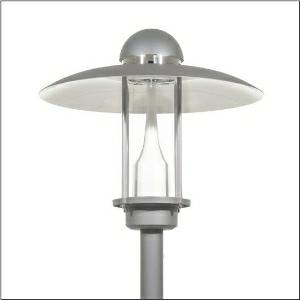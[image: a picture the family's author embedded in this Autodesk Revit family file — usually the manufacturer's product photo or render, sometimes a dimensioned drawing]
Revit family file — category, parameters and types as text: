
# Revit family: city-light_elegance_iq___p1_0a_5xa5265nf14hp_aba6
name_source: partatom
category: Lighting Fixtures
units: mm (PartAtom-declared; Revit-internal decimal feet)

## family parameters
Cut with Voids When Loaded = No
Host = Face
Light Source = No
Part Type = Normal
Room Calculation Point = No
Round Connector Dimension = Use Diameter
Shared = No

## types (1)
- --- (1 x LED, 4020 lm, 33.6 W, 2700K)
    Apparent Load = 34 VA
    CIE Flux Codes = 31 62 91 97 100
    Color Rendering = 70
    Color Temperature = 2700K
    Default Elevation = 1800 mm
    Description = City-Light Elegance iQ, mast luminaire, Module 540 iQ-SR, primary light control with 3 zone facetted reflector, of plastic, silver coated, highly specular, structured, primary optical cover: cover, of PMMA, transparent, light distribution: P1.0a, light emission: direct distribution, primary light characteristic: strongly asymmetric, installation type: post-top, LED, High Power LED, rated luminous flux: 4.020lm, luminous efficacy: 120lm/W, light colour: 727, colour temperature: 2700K, control gear: iQ Street-Remote, control: pre-setting: logarithmic dimming characteristic, Street-Remote, Auto-Match, Temp-Guard, Lumen-Switch, Night-Set, Smart-Wire, Light-Fading, Desk-Remote (wireless, voltage-free reading and setting of iQ features in the workshop via application-optimized NFC function/RFID function), optimised constant luminous flux control (CLO 2.0), with terminal, 6-pole, max. 2.5mm², mains connection: 230..240V, AC, 50/60Hz, start of lifetime: 34W, end of service life: 36W, reduction: 15W, luminaire housing, upper part, of aluminium, coated, Siteco® metallic grey (DB 702S), diameter: 750mm, height: 675mm, spigot size: d x l = 76 x 70mm (post-top) | with reducer (optional accessory) 60 x 70mm, mounting height: 3..5m, post-top mast mounting element, of diecast aluminium, coated, Siteco® metallic grey (DB 702S), Module 540 iQ-SR, traffic white (RAL 9016), equipment: Power, protection rating (complete): IP65, insulation class (complete): insulation class II (safety insulation), certification: CE, ENEC, VDE, packaging unit: 1 piece

Light Distribution: P1.0a
    Height = 675 mm
    Lamp = 1 x LED
    Lamp Light Flux = 4020 lm
    Lamp Power = 33.6 W
    Lamp count = 1
    Length = 750 mm
    Luminous efficacy = 120 lm/W
    Manufacturer = Siteco
    ModVariant = No
    Model = 5XA5265NF14HP
    Number of Poles = 1
    OnlyDefault = Yes
    Power Factor = 1
    Product Name = City-Light Elegance iQ | P1.0a
    Product group = mast luminaire | pylon top
    ProductGroupID = 6100
    Protection Class = Protection class II
    Protection Degree = IP 65
    RLX_Detail_Level = 1
    RLX_Emergency_Light_Flux = 0 lm
    RLX_Emergency_Type = 0
    RLX_Emergency_Type_DB = No
    RlxData = <blob elided: 36865 chars, md5=34d14fb5>
    Socket = socket
    Standby Power = 0 W
    System Light Flux = 4020 lm
    System Power = 34 W
    Type Comments = factory setting: luminous flux: 100 % | dim-lin: 254 | 695 mA
    Type Image = l_1006912.jpg
    URL = http://relux.com
    VarID = @adj_152580
    Voltage = 0 V
    Weight = 0.00 kg
    Width = 0 mm  [stored 0 ft]

note: [stored X ft] marks values corroborated as IEEE doubles in the binary element streams (Revit-internal decimal feet)

## geometry (parser evidence)
native form markers: Blend x4, Sweep x12
no freeform markers — native parametric forms only
